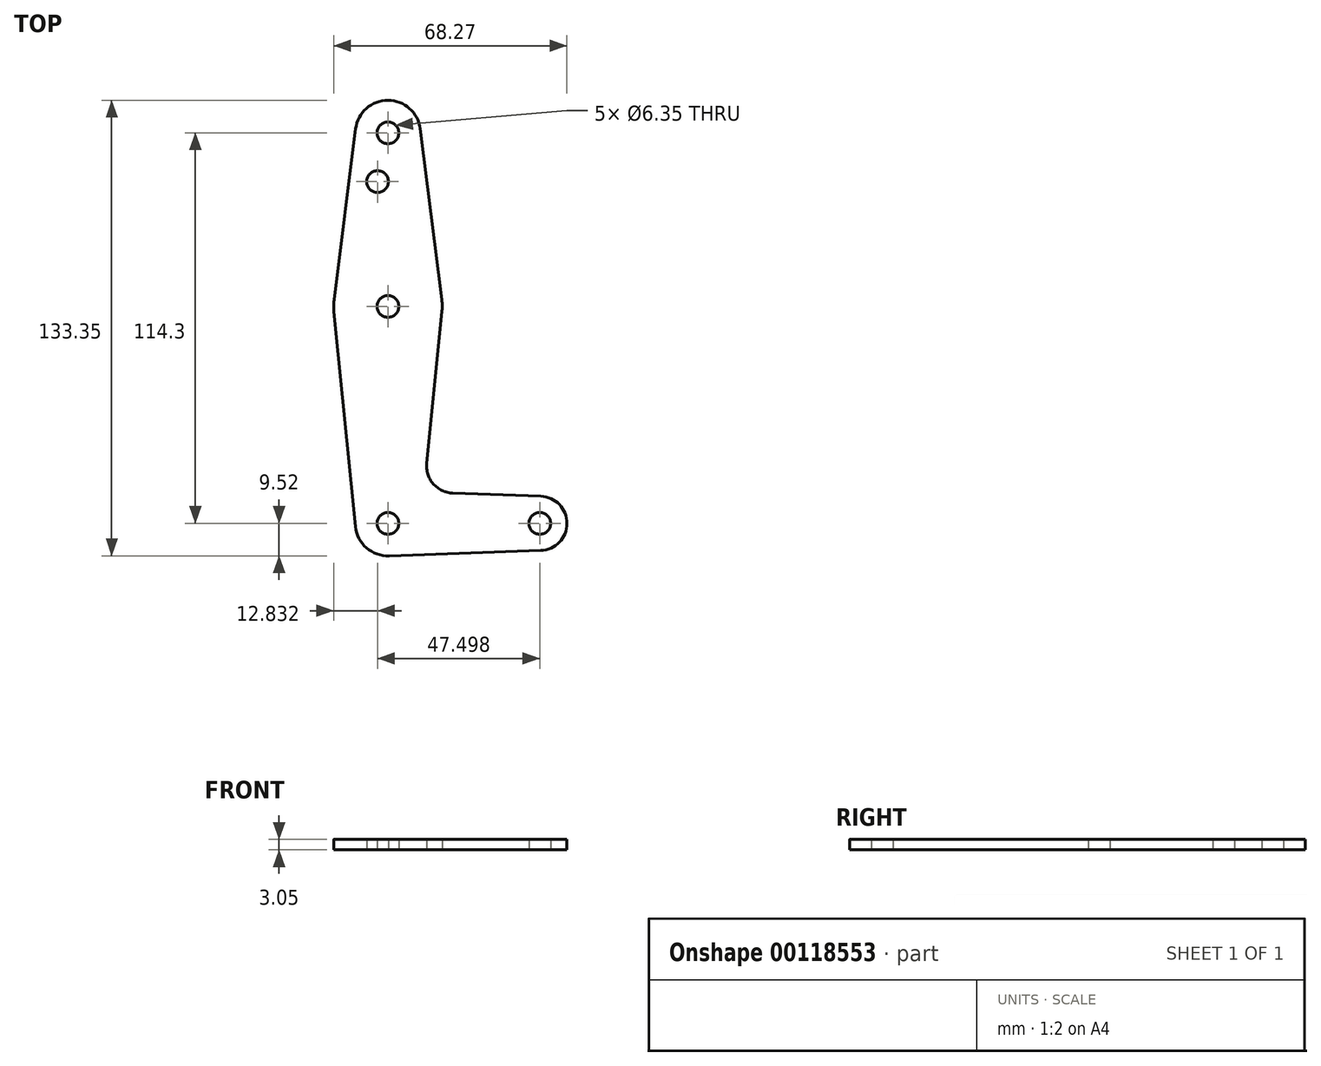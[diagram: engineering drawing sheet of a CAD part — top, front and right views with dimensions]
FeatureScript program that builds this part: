
annotation { "Feature Type Name" : "Feature", "Feature Type Description" : "" }
export const myFeature = defineFeature(function(context is Context, id is Id, definition is map)
    precondition{}
    {
        {
            var Q0;
            Q0=qCreatedBy(makeId("Top.planeOp"),FACE);
            var sketch = newSketch(context, id + "F0", { "sketchPlane" : qUnion([Q0])});
            skLineSegment(sketch, "E0", {"start": v(0, 0) * mm, "end": v(0, 114.3) * mm, "construction": true});
            skLineSegment(sketch, "E1", {"start": v(0, 0) * mm, "end": v(44.45, 0) * mm, "construction": true});
            skCircle(sketch, "E2", {"center": v(0, 114.3) * mm, "radius": 9.53 * mm});
            skCircle(sketch, "E3", {"center": v(0, 0) * mm, "radius": 9.53 * mm});
            skCircle(sketch, "E4", {"center": v(44.45, 0) * mm, "radius": 7.94 * mm});
            skCircle(sketch, "E5", {"center": v(0, 63.5) * mm, "radius": 15.88 * mm});
            skCircle(sketch, "E6", {"center": v(-3.05, 100.03) * mm, "radius": 3.18 * mm});
            skCircle(sketch, "E7", {"center": v(0, 114.3) * mm, "radius": 3.18 * mm});
            skCircle(sketch, "E8", {"center": v(0, 63.5) * mm, "radius": 3.18 * mm});
            skCircle(sketch, "E9", {"center": v(0, 0) * mm, "radius": 3.18 * mm});
            skCircle(sketch, "E10", {"center": v(44.45, 0) * mm, "radius": 3.18 * mm});
            skLineSegment(sketch, "E11", {"start": v(9.45, 115.5) * mm, "end": v(15.75, 65.48) * mm});
            skLineSegment(sketch, "E12", {"start": v(15.8, 61.91) * mm, "end": v(11.34, 17.6) * mm});
            skLineSegment(sketch, "E13", {"start": v(-15.8, 61.91) * mm, "end": v(-9.48, -0.95) * mm});
            skLineSegment(sketch, "E14", {"start": v(0.34, -9.52) * mm, "end": v(44.73, -7.93) * mm});
            skLineSegment(sketch, "E15", {"start": v(18.97, 8.85) * mm, "end": v(44.73, 7.93) * mm});
            skLineSegment(sketch, "E16", {"start": v(-15.75, 65.48) * mm, "end": v(-9.45, 115.5) * mm});
            skArc(sketch, "E17.filletArc", {"start": v(11.34, 17.6) * mm, "mid": v(13.26, 11.57) * mm, "end": v(18.97, 8.85) * mm});
            skSolve(sketch);
        }
        {
            var Q0;
            Q0 = qSketchRegion(id + "F0", true);
            extrude(context, id + "F1", {"entities" : qUnion([Q0]), "depth" : 3.05 * mm});
        }
    });
